# Revit family: N167e
name_source: partatom
category: Generic Models
revit_build: Autodesk Revit 2018 (Build: 20170223_1515(x64)
units: mm (PartAtom-declared; Revit-internal decimal feet)

## family parameters
Can host rebar = No
Cut with Voids When Loaded = No
Host = Face
Part Type = Normal
Room Calculation Point = No
Round Connector Dimension = Use Diameter
Shared = No

## types (1)
- N167e
    Default Elevation = 1219 mm
    Description = Demand Direct N167e Commercial System
    Gas Manifold Size = 32 mm  [stored 0.104987 ft]
    Hot & Cold Manifold Distance from Upright = 16 mm  [stored 0.0524934 ft]
    Hot & Cold Manifold Sizes = 32 mm  [stored 0.104987 ft]
    Manufacturer = Rinnai NZ
    Model = RCWN167eN/L (Natural Gas or LPG)
    URL = https://rinnai.co.nz

note: [stored X ft] marks values corroborated as IEEE doubles in the binary element streams (Revit-internal decimal feet)

## geometry (parser evidence)
native form markers: Sweep x12
no freeform markers — native parametric forms only
